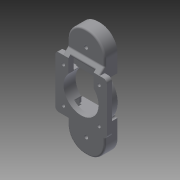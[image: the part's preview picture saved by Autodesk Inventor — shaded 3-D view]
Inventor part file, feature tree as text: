
AUTODESK INVENTOR PART (.ipt)
format: ipt  version: 2014 (Build 180170000, 170)  size: 476,672 bytes
history: native  units: in
note: dims shown in document units (in); Inventor stores cm internally (conversion verified against a paired STEP export)
features: extrude x10, sketch x9, reference x9, fillet x7, projected_geometry x2, plane x1, chamfer x1
ambient origin geometry x8: Origin, YZ Plane, XZ Plane, XY Plane, X Axis, Y Axis, Z Axis, Center Point
bodies: Solid1 (feature_tree)
feature tree (39):
  plane  "Work Plane1"
  extrude  "Extrusion1"  Depth=3.73in
  extrude  "Extrusion3"  Depth=0.864in
  extrude  "Extrusion5"  Depth=1.7717in
  extrude  "Extrusion6"  Depth=0.1732in TaperAngle=0.0deg
  extrude  "Extrusion7"  Depth=0.125in
  extrude  "Extrusion8"  Depth=0.125in
  extrude  "Extrusion10"  Depth=0.125in
  extrude  "Extrusion11"  Depth=0.125in
  fillet  "Fillet1"  Radius=0.25in
  extrude  "Extrusion12"  Depth=0.125in
  chamfer  "Chamfer1"  Distance=0.3in
  fillet  "Fillet2"  Radius=0.18in
  fillet  "Fillet3"  Radius=0.1339in
  fillet  "Fillet4"  Radius=0.1339in
  fillet  "Fillet5"  Radius=0.0118in
  extrude  "Extrusion13"  Depth=0.125in
  fillet  "Fillet6"  [1 undecoded]
  fillet  "Fillet7"  Radius=0.125in
  sketch  "Sketch1"  dims[d0=1.27in d1=3.73in]
  reference  "Reference1"
  sketch  "Sketch2"  dims[d2=0.2in d3=0.0in d4=0.864in]
  reference  "Reference2"
  reference  "Reference3"
  reference  "Reference4"
  reference  "Reference5"
  reference  "Reference6"
  reference  "Reference7"
  reference  "Reference8"
  reference  "Reference9"
  projected_geometry  "Projected Loop1"
  sketch  "Sketch4"  dims[d7=0.239in d8=0.0in d9=1.7717in]
  sketch  "Sketch6"  dims[d10=1.7717in d19=0.1732in d20=0.0in]
  sketch  "Sketch7"  dims[d21=0.1732in d22=0.0in d23=0.125in]
  sketch  "Sketch8"  dims[d25=0.125in d26=0.18in]
  projected_geometry  "Projected Loop2"
  sketch  "Sketch9"  dims[d27=0.125in d28=0.25in]
  sketch  "Sketch10"  dims[d29=0.3in d30=0.0in d31=0.125in d32=0.25in]
  sketch  "Sketch11"  dims[d33=0.125in d34=0.125in d35=0.3in d36=0.0in d37=0.18in d38=0.1339in d39=0.1339in d42=0.0118in d43=0.0in d44=1.2in d45=0.0in d46=0.0in d47=0.125in d48=0.173in d49=0.173in d50=0.0in d51=0.173in d52=0.125in d53=45.0deg d54=0.05in d55=0.6in d56=0.06in d57=0.06in d58=0.15in d59=1.0in d60=0.0in d61=0.0394in d62=1.2205in d63=1.2205in d68=0.1181in d69=0.1181in d70=0.1181in d71=0.1181in d72=0.4538in d73=0.1444in d74=0.1444in d75=0.125in]
note: 1 required parameter value undecoded (feature->parameter linkage not recoverable at this tier; creation-order binding heuristic only, values carry confidence <= 0.55)
